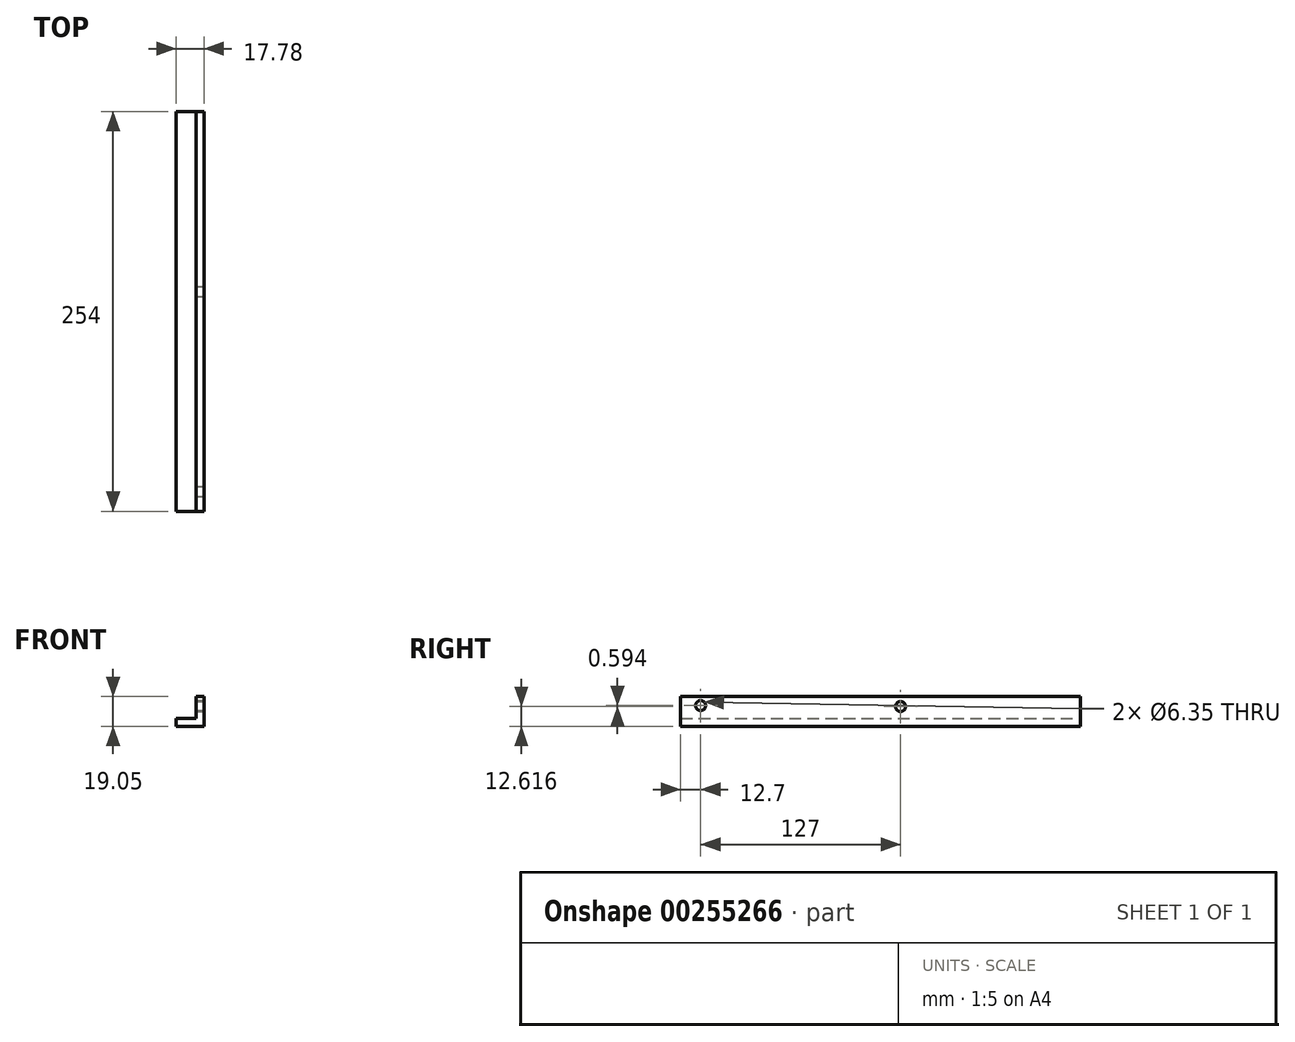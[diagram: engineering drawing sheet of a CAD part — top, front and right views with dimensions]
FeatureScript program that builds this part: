
annotation { "Feature Type Name" : "Feature", "Feature Type Description" : "" }
export const myFeature = defineFeature(function(context is Context, id is Id, definition is map)
    precondition{}
    {
        {
            var Q0;
            Q0=qCreatedBy(makeId("Front.planeOp"),FACE);
            var sketch = newSketch(context, id + "F0", { "sketchPlane" : qUnion([Q0])});
            skLineSegment(sketch, "E0", {"start": v(0, 0) * mm, "end": v(0, 19.05) * mm});
            skLineSegment(sketch, "E1", {"start": v(0, 19.05) * mm, "end": v(-5.08, 19.05) * mm});
            skLineSegment(sketch, "E2", {"start": v(-5.08, 19.05) * mm, "end": v(-5.08, 5.08) * mm});
            skLineSegment(sketch, "E3", {"start": v(-5.08, 5.08) * mm, "end": v(-17.78, 5.08) * mm});
            skLineSegment(sketch, "E4", {"start": v(-17.78, 5.08) * mm, "end": v(-17.78, 0) * mm});
            skLineSegment(sketch, "E5", {"start": v(-17.78, 0) * mm, "end": v(0, 0) * mm});
            skSolve(sketch);
        }
        {
            var Q0;
            Q0 = qSketchRegion(id + "F0", true);
            extrude(context, id + "F1", {"entities" : qUnion([Q0]), "depth" : 254 * mm});
        }
        {
            var Q0;
            Q0=makeQuery(id+"F1.opExtrude","SWEPT_FACE",FACE,{"disambiguationData":[OSD([sQuery(id+"F0.wireOp",EDGE,"E0")])]});
            var sketch = newSketch(context, id + "F2", { "sketchPlane" : qUnion([Q0])});
            skCircle(sketch, "E6", {"center": v(-241.3, 13.2) * mm, "radius": 3.18 * mm});
            skCircle(sketch, "E7", {"center": v(-114.3, 12.62) * mm, "radius": 3.18 * mm});
            skSolve(sketch);
        }
        {
            var Q0;
            Q0 = qSketchRegion(id + "F2", true);
            extrude(context, id + "F3", {"entities" : qUnion([Q0]), "operationType" : NewBodyOperationType.REMOVE, "oppositeDirection" : true, "depth" : 25.4 * mm});
        }
    });
